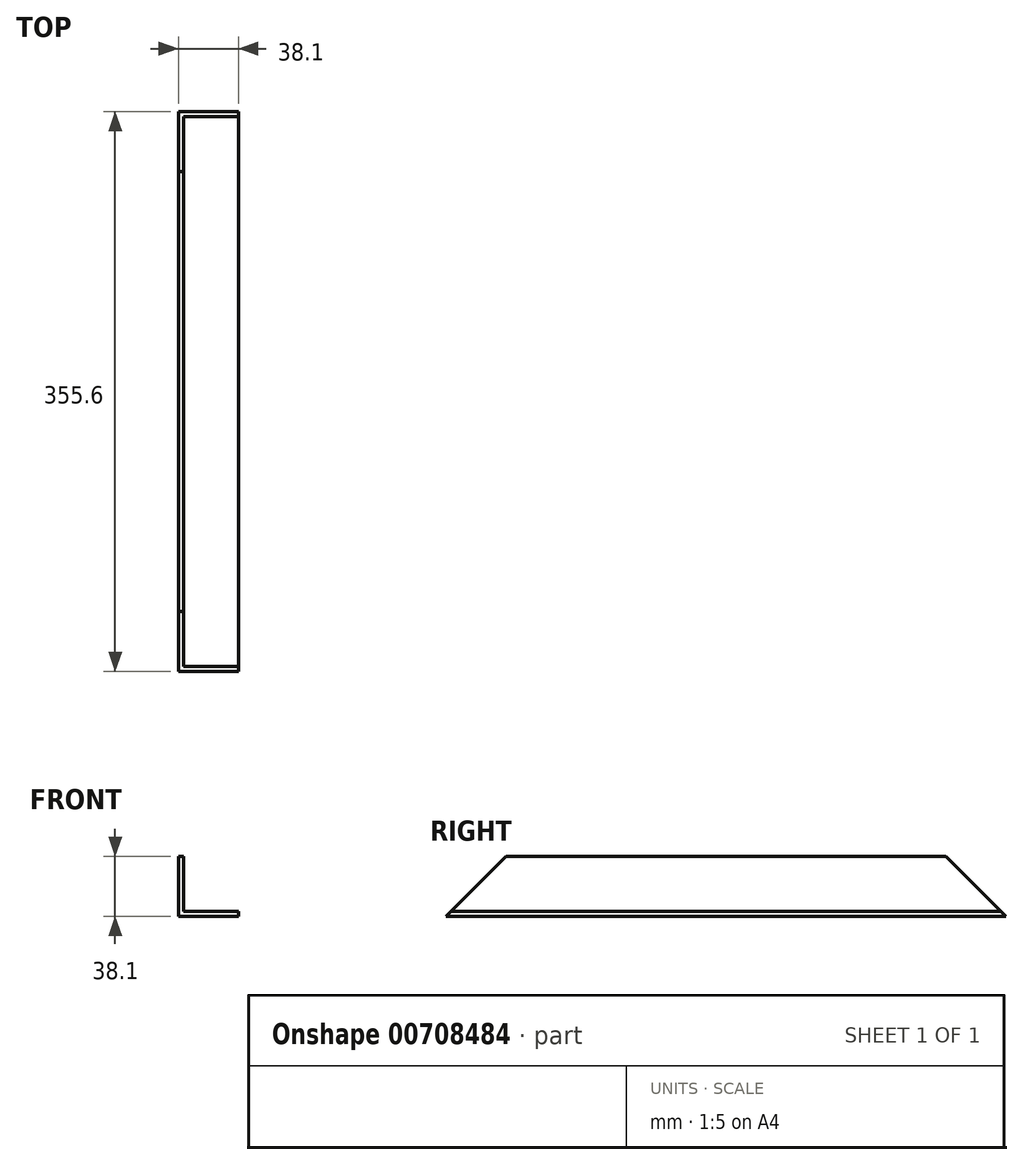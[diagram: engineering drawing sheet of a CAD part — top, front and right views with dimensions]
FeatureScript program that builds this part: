
annotation { "Feature Type Name" : "Feature", "Feature Type Description" : "" }
export const myFeature = defineFeature(function(context is Context, id is Id, definition is map)
    precondition{}
    {
        {
            var Q0;
            Q0=qCreatedBy(makeId("Front.planeOp"),FACE);
            var sketch = newSketch(context, id + "F0", { "sketchPlane" : qUnion([Q0])});
            skLineSegment(sketch, "E0", {"start": v(0, 0) * mm, "end": v(38.1, 0) * mm});
            skLineSegment(sketch, "E1", {"start": v(0, 0) * mm, "end": v(0, 38.1) * mm});
            skLineSegment(sketch, "E2.0", {"start": v(3.18, 3.18) * mm, "end": v(38.1, 3.18) * mm});
            skLineSegment(sketch, "E2.1", {"start": v(3.18, 3.18) * mm, "end": v(3.18, 38.1) * mm});
            skLineSegment(sketch, "E3", {"start": v(38.1, 0) * mm, "end": v(38.1, 3.18) * mm});
            skLineSegment(sketch, "E4", {"start": v(0, 38.1) * mm, "end": v(3.18, 38.1) * mm});
            skSolve(sketch);
        }
        {
            var Q0;
            Q0 = qSketchRegion(id + "F0", true);
            extrude(context, id + "F1", {"entities" : qUnion([Q0]), "depth" : 355.6 * mm, "offsetDistance" : 25.4 * mm});
        }
        {
            var Q0;
            Q0=makeQuery(id+"F1.opExtrude","SWEPT_FACE",FACE,{"disambiguationData":[OSD([sQuery(id+"F0.wireOp",EDGE,"E1")])]});
            var sketch = newSketch(context, id + "F2", { "sketchPlane" : qUnion([Q0])});
            skLineSegment(sketch, "E5.0", {"start": v(355.6, 0) * mm, "end": v(355.6, 38.1) * mm});
            skLineSegment(sketch, "E5.1", {"start": v(355.6, 38.1) * mm, "end": v(317.5, 38.1) * mm});
            skLineSegment(sketch, "E6", {"start": v(355.6, 0) * mm, "end": v(317.5, 38.1) * mm});
            skPoint(sketch, "E7.orphan", {"position": v(0, 38.1) * mm});
            skLineSegment(sketch, "E8.1", {"start": v(0, 0) * mm, "end": v(0, 38.1) * mm});
            skLineSegment(sketch, "E9", {"start": v(0, 0) * mm, "end": v(38.1, 38.1) * mm});
            skLineSegment(sketch, "E10.trimOffspring", {"start": v(38.1, 38.1) * mm, "end": v(0, 38.1) * mm});
            skSolve(sketch);
        }
        {
            var Q0;
            Q0 = qSketchRegion(id + "F2", true);
            extrude(context, id + "F3", {"entities" : qUnion([Q0]), "operationType" : NewBodyOperationType.REMOVE, "endBound" : BoundingType.THROUGH_ALL, "oppositeDirection" : true, "depth" : 25.4 * mm, "offsetDistance" : 25.4 * mm});
        }
    });
